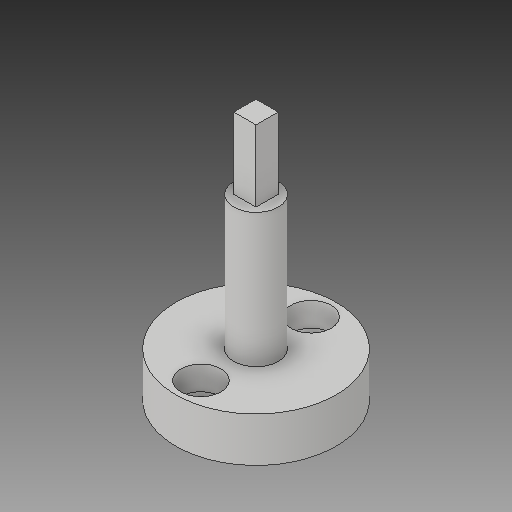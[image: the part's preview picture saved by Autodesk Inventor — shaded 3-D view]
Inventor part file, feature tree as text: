
AUTODESK INVENTOR PART (.ipt)
format: ipt  version: 2019 (Build 230136000, 136)  size: 139,776 bytes
history: native  units: in
note: dims shown in document units (in); Inventor stores cm internally (conversion verified against a paired STEP export)
features: sketch x4, extrude x3, hole x1
ambient origin geometry x8: Origin, YZ Plane, XZ Plane, XY Plane, X Axis, Y Axis, Z Axis, Center Point
bodies: Solid1 (feature_tree)
feature tree (8):
  extrude  "Extrusion1"  Depth=0.25in TaperAngle=0.0deg
  hole  "Hole1"  [1 undecoded]
  extrude  "Extrusion2"  Depth=0.25in
  extrude  "Extrusion3"  Depth=0.125in
  sketch  "Sketch1"  dims[d0=0.9in d1=0.25in d2=0.0in]
  sketch  "Sketch2"  dims[d3=0.6185in d4=0.3093in]
  sketch  "Sketch3"  dims[d5=0.134in d6=0.75in d7=0.225in d8=0.135in d9=0.5635in d10=0.4in d11=0.0in d12=0.25in]
  sketch  "Sketch4"  dims[d13=0.75in d14=0.0in d15=0.125in d16=0.125in d17=0.0625in d18=0.0625in d19=0.4in d20=0.0in d21=0.3093in d22=0.0in]
note: 1 required parameter value undecoded (feature->parameter linkage not recoverable at this tier; creation-order binding heuristic only, values carry confidence <= 0.55)
